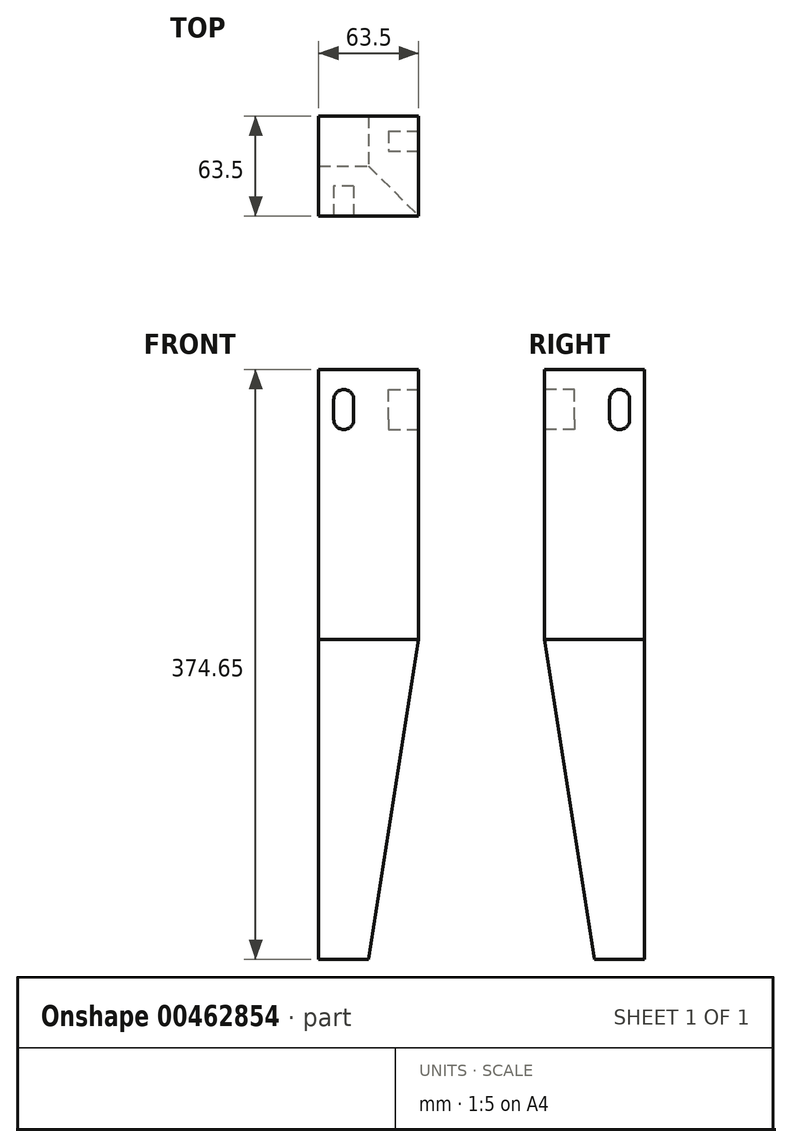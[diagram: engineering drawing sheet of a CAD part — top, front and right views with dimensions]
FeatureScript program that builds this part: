
annotation { "Feature Type Name" : "Feature", "Feature Type Description" : "" }
export const myFeature = defineFeature(function(context is Context, id is Id, definition is map)
    precondition{}
    {
        {
            var Q0;
            Q0=qCreatedBy(makeId("Top.planeOp"),FACE);
            var sketch = newSketch(context, id + "F0", { "sketchPlane" : qUnion([Q0])});
            skLineSegment(sketch, "E0.bottom", {"start": v(-31.75, -31.75) * mm, "end": v(31.75, -31.75) * mm});
            skLineSegment(sketch, "E0.top", {"start": v(-31.75, 31.75) * mm, "end": v(31.75, 31.75) * mm});
            skLineSegment(sketch, "E0.left", {"start": v(-31.75, -31.75) * mm, "end": v(-31.75, 31.75) * mm});
            skLineSegment(sketch, "E0.right", {"start": v(31.75, -31.75) * mm, "end": v(31.75, 31.75) * mm});
            skLineSegment(sketch, "E1", {"start": v(-31.75, -31.75) * mm, "end": v(31.75, 31.75) * mm, "construction": true});
            skSolve(sketch);
        }
        {
            var Q0;
            Q0=makeQuery(id+"F0.imprint","IMPRINT",FACE,{"disambiguationData":[TD([[makeQuery(id+"F0.imprint","IMPRINT",EDGE,{"derivedFrom":sQuery(id+"F0.wireOp",EDGE,"E0.bottom")}),1.0]])]});
            extrude(context, id + "F1", {"entities" : qUnion([Q0]), "oppositeDirection" : true, "depth" : 171.45 * mm});
        }
        {
            var Q0;
            Q0=makeQuery(id+"F1.opExtrude","CAP_FACE",FACE,{"disambiguationData":[OSD([sQuery(id+"F0.wireOp",EDGE,"E0.bottom"),sQuery(id+"F0.wireOp",EDGE,"E0.top"),sQuery(id+"F0.wireOp",EDGE,"E0.left"),sQuery(id+"F0.wireOp",EDGE,"E0.right")])],"isStart":false});
            cPlane(context, id + "F2", {"entities" : qUnion([Q0]), "cplaneType" : CPlaneType.OFFSET, "offset" : 203.2 * mm, "width" : 152.4 * mm, "height" : 152.4 * mm});
        }
        {
            var Q0;
            Q0=qCreatedBy(id+"F2.planeOp",FACE);
            var sketch = newSketch(context, id + "F3", { "sketchPlane" : qUnion([Q0])});
            skLineSegment(sketch, "E2.bottom", {"start": v(-31.75, -31.75) * mm, "end": v(0, -31.75) * mm});
            skLineSegment(sketch, "E2.top", {"start": v(-31.75, 0) * mm, "end": v(0, 0) * mm});
            skLineSegment(sketch, "E2.left", {"start": v(-31.75, -31.75) * mm, "end": v(-31.75, 0) * mm});
            skLineSegment(sketch, "E2.right", {"start": v(0, -31.75) * mm, "end": v(0, 0) * mm});
            skPoint(sketch, "E3.0", {"position": v(-31.75, -31.75) * mm});
            skSolve(sketch);
        }
        {
            var Q1;
            Q1 = qSketchRegion(id + "F3", true);
            var Q2;
            Q2=makeQuery(id+"F1.opExtrude","CAP_FACE",FACE,{"disambiguationData":[OSD([sQuery(id+"F0.wireOp",EDGE,"E0.bottom"),sQuery(id+"F0.wireOp",EDGE,"E0.top"),sQuery(id+"F0.wireOp",EDGE,"E0.left"),sQuery(id+"F0.wireOp",EDGE,"E0.right")])],"isStart":false});
            loft(context, id + "F4", {"operationType" : NewBodyOperationType.ADD, "sheetProfilesArray" : [{ "sheetProfileEntities" : qUnion([Q1]) }, { "sheetProfileEntities" : qUnion([Q2]) }]});
        }
        {
            var Q0;
            Q0=makeQuery(id+"F1.opExtrude","SWEPT_FACE",FACE,{"disambiguationData":[OSD([sQuery(id+"F0.wireOp",EDGE,"E0.bottom")])]});
            var sketch = newSketch(context, id + "F5", { "sketchPlane" : qUnion([Q0])});
            skPoint(sketch, "E4.0", {"position": v(-31.75, 0) * mm});
            skLineSegment(sketch, "E5.bottom", {"start": v(-22.22, -31.75) * mm, "end": v(-9.52, -31.75) * mm, "construction": true});
            skLineSegment(sketch, "E5.top", {"start": v(-22.22, -19.05) * mm, "end": v(-9.52, -19.05) * mm, "construction": true});
            skLineSegment(sketch, "E5.left", {"start": v(-22.22, -31.75) * mm, "end": v(-22.22, -19.05) * mm});
            skLineSegment(sketch, "E5.right", {"start": v(-9.52, -31.75) * mm, "end": v(-9.52, -19.05) * mm});
            skArc(sketch, "E6", {"start": v(-9.52, -19.05) * mm, "mid": v(-15.87, -12.7) * mm, "end": v(-22.22, -19.05) * mm});
            skArc(sketch, "E7", {"start": v(-22.22, -31.75) * mm, "mid": v(-15.87, -38.1) * mm, "end": v(-9.52, -31.75) * mm});
            skSolve(sketch);
        }
        {
            var Q0;
            Q0 = qSketchRegion(id + "F5", true);
            extrude(context, id + "F6", {"entities" : qUnion([Q0]), "operationType" : NewBodyOperationType.REMOVE, "oppositeDirection" : true, "depth" : 19.05 * mm});
        }
        {
            var Q0;
            Q0=makeQuery(id+"F1.opExtrude","SWEPT_FACE",FACE,{"disambiguationData":[OSD([sQuery(id+"F0.wireOp",EDGE,"E0.right")])]});
            var sketch = newSketch(context, id + "F7", { "sketchPlane" : qUnion([Q0])});
            skPoint(sketch, "E8.0", {"position": v(31.75, 0) * mm});
            skLineSegment(sketch, "E9.bottom", {"start": v(9.53, -31.75) * mm, "end": v(22.23, -31.75) * mm, "construction": true});
            skLineSegment(sketch, "E9.top", {"start": v(9.53, -19.05) * mm, "end": v(22.22, -19.05) * mm, "construction": true});
            skLineSegment(sketch, "E9.left", {"start": v(9.53, -31.75) * mm, "end": v(9.53, -19.05) * mm});
            skLineSegment(sketch, "E9.right", {"start": v(22.23, -31.75) * mm, "end": v(22.23, -19.05) * mm});
            skArc(sketch, "E10", {"start": v(22.22, -19.05) * mm, "mid": v(15.87, -12.7) * mm, "end": v(9.52, -19.05) * mm});
            skArc(sketch, "E11", {"start": v(9.52, -31.75) * mm, "mid": v(15.88, -38.1) * mm, "end": v(22.23, -31.75) * mm});
            skSolve(sketch);
        }
        {
            var Q0;
            Q0 = qSketchRegion(id + "F7", true);
            extrude(context, id + "F8", {"entities" : qUnion([Q0]), "operationType" : NewBodyOperationType.REMOVE, "oppositeDirection" : true, "depth" : 19.05 * mm});
        }
    });
